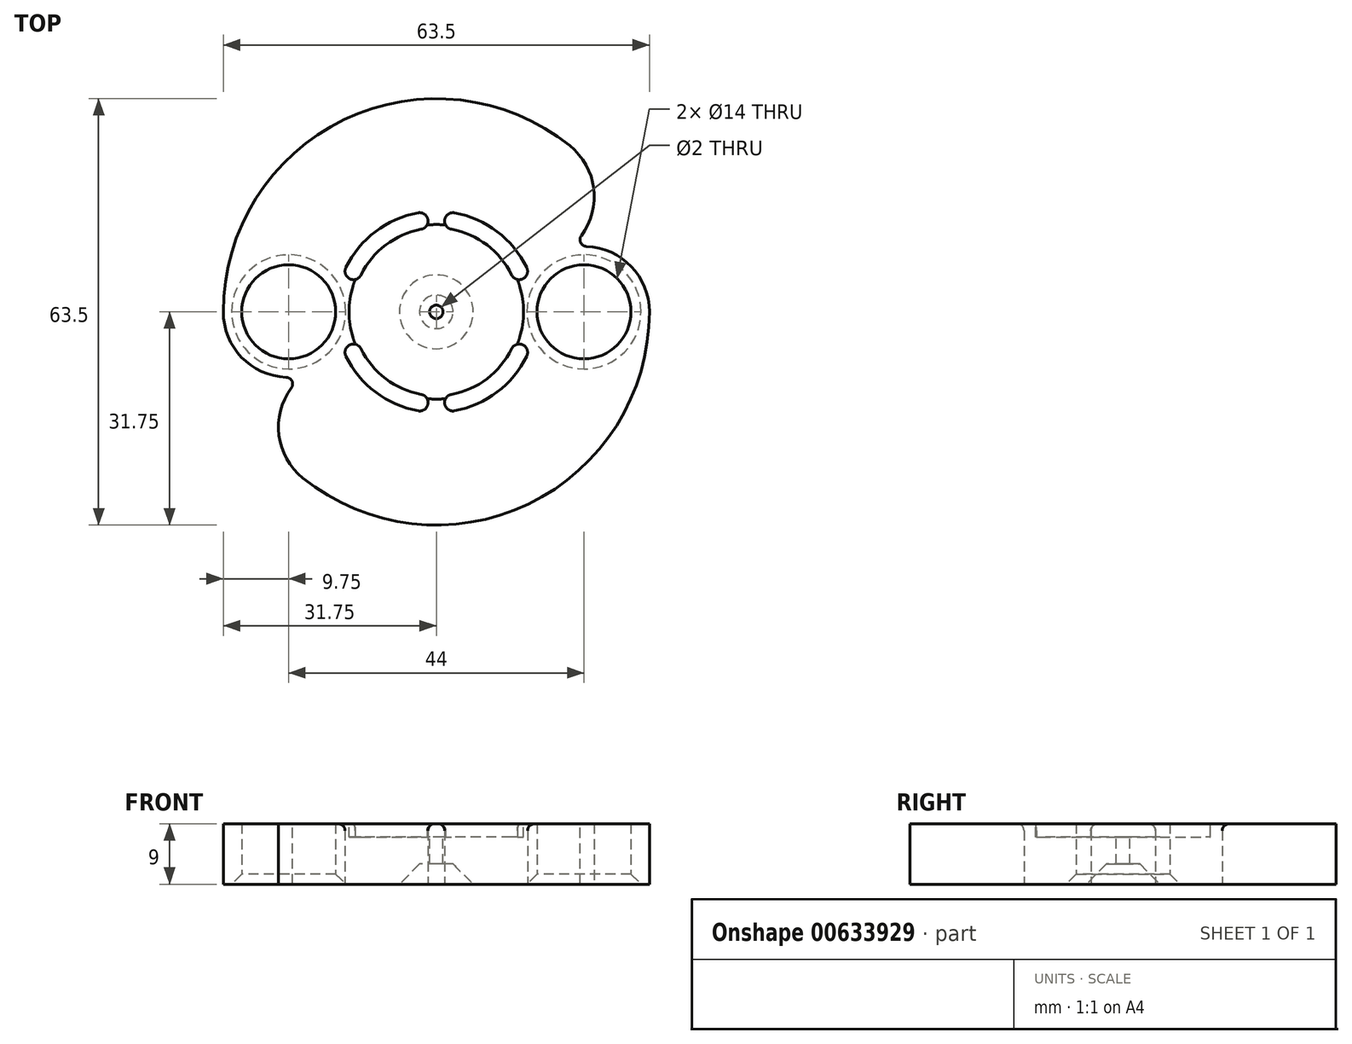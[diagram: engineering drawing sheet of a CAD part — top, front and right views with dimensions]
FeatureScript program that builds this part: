
annotation { "Feature Type Name" : "Feature", "Feature Type Description" : "" }
export const myFeature = defineFeature(function(context is Context, id is Id, definition is map)
    precondition{}
    {
        {
            var Q0;
            Q0=qCreatedBy(makeId("Top.planeOp"),FACE);
            var sketch = newSketch(context, id + "F0", { "sketchPlane" : qUnion([Q0])});
            skCircle(sketch, "E0", {"center": v(0, 0) * mm, "radius": 32.5 * mm});
            skCircle(sketch, "E1", {"center": v(0, 0) * mm, "radius": 2.5 * mm});
            skCircle(sketch, "E2", {"center": v(22, 0) * mm, "radius": 7 * mm});
            skLineSegment(sketch, "E3", {"start": v(0, 0) * mm, "end": v(22, 0) * mm, "construction": true});
            skLineSegment(sketch, "E4", {"start": v(0, 0) * mm, "end": v(-22, 0) * mm, "construction": true});
            skCircle(sketch, "E5", {"center": v(-22, 0) * mm, "radius": 7 * mm});
            skSolve(sketch);
        }
        {
            var Q0;
            Q0 = qSketchRegion(id + "F0", true);
            extrude(context, id + "F1", {"entities" : qUnion([Q0]), "endBound" : BoundingType.SYMMETRIC, "depth" : 9 * mm, "offsetDistance" : 25 * mm});
        }
        {
            var Q0;
            Q0=makeQuery(id+"F1.opExtrude","CAP_FACE",FACE,{"disambiguationData":[OSD([sQuery(id+"F0.wireOp",EDGE,"E0"),sQuery(id+"F0.wireOp",EDGE,"E1"),sQuery(id+"F0.wireOp",EDGE,"E2")])],"isStart":false});
            var sketch = newSketch(context, id + "F2", { "sketchPlane" : qUnion([Q0])});
            skCircle(sketch, "E6", {"center": v(0, 0) * mm, "radius": 1 * mm});
            skCircle(sketch, "E7", {"center": v(0, 0) * mm, "radius": 2.5 * mm});
            skSolve(sketch);
        }
        {
            var Q0;
            Q0 = qSketchRegion(id + "F2", true);
            extrude(context, id + "F3", {"entities" : qUnion([Q0]), "operationType" : NewBodyOperationType.ADD, "oppositeDirection" : true, "depth" : 6 * mm, "offsetDistance" : 25 * mm});
        }
        {
            var Q0;
            Q0=makeQuery(id+"F1.opExtrude","CAP_FACE",FACE,{"disambiguationData":[OSD([sQuery(id+"F0.wireOp",EDGE,"E0"),sQuery(id+"F0.wireOp",EDGE,"E1"),sQuery(id+"F0.wireOp",EDGE,"E2")])],"isStart":true});
            var sketch = newSketch(context, id + "F4", { "sketchPlane" : qUnion([Q0])});
            skLineSegment(sketch, "E8", {"start": v(0, 0) * mm, "end": v(22, 0) * mm, "construction": true});
            skCircle(sketch, "E9", {"center": v(0, 0) * mm, "radius": 32.5 * mm});
            skArc(sketch, "E10", {"start": v(12.25, 0) * mm, "mid": v(5.3, 11.05) * mm, "end": v(-7.67, 9.55) * mm});
            skArc(sketch, "E11", {"start": v(31.75, 0) * mm, "mid": v(13.72, 28.63) * mm, "end": v(-19.9, 24.75) * mm});
            skLineSegment(sketch, "E12", {"start": v(0, 0) * mm, "end": v(-22, 0) * mm, "construction": true});
            skArc(sketch, "E13", {"start": v(-12.25, 0) * mm, "mid": v(-22, 9.75) * mm, "end": v(-31.75, 0) * mm});
            skArc(sketch, "E14", {"start": v(12.25, 0) * mm, "mid": v(22, -9.75) * mm, "end": v(31.75, 0) * mm});
            skCircle(sketch, "E15", {"center": v(0, 0) * mm, "radius": 22 * mm, "construction": true});
            skArc(sketch, "E16", {"start": v(-15.94, 7.64) * mm, "mid": v(-11.6, 7.65) * mm, "end": v(-7.67, 9.55) * mm});
            skArc(sketch, "E17.trimOffspring", {"start": v(-19.9, 24.75) * mm, "mid": v(-23.53, 17.12) * mm, "end": v(-19.84, 9.5) * mm});
            skArc(sketch, "E18", {"start": v(15.94, -7.64) * mm, "mid": v(11.6, -7.65) * mm, "end": v(7.67, -9.55) * mm});
            skArc(sketch, "E19.trimOffspring", {"start": v(19.9, -24.75) * mm, "mid": v(23.53, -17.12) * mm, "end": v(19.84, -9.5) * mm});
            skArc(sketch, "E20.trimOffspring", {"start": v(-12.25, 0) * mm, "mid": v(-5.3, -11.05) * mm, "end": v(7.67, -9.55) * mm});
            skArc(sketch, "E21.trimOffspring", {"start": v(-31.75, 0) * mm, "mid": v(-13.72, -28.63) * mm, "end": v(19.9, -24.75) * mm});
            skSolve(sketch);
        }
        {
            var Q0;
            Q0 = qSketchRegion(id + "F4", true);
            extrude(context, id + "F5", {"entities" : qUnion([Q0]), "operationType" : NewBodyOperationType.REMOVE, "oppositeDirection" : true, "depth" : 5 * mm, "offsetDistance" : 25 * mm});
        }
        {
            var Q0;
            Q0=makeQuery(id+"F3.boolean.opBoolean","MERGE",FACE,{"derivedFrom":[makeQuery(id+"F1.opExtrude","CAP_FACE",FACE,{"disambiguationData":[OSD([sQuery(id+"F0.wireOp",EDGE,"E0"),sQuery(id+"F0.wireOp",EDGE,"E1"),sQuery(id+"F0.wireOp",EDGE,"E2")])],"isStart":false}),makeQuery(id+"F3.opExtrude","CAP_FACE",FACE,{"disambiguationData":[OSD([sQuery(id+"F2.wireOp",EDGE,"E6"),sQuery(id+"F2.wireOp",EDGE,"E7")])],"isStart":true})]});
            var sketch = newSketch(context, id + "F6", { "sketchPlane" : qUnion([Q0])});
            skCircle(sketch, "E22", {"center": v(0, 0) * mm, "radius": 13 * mm});
            skSolve(sketch);
        }
        {
            var Q0;
            Q0 = qSketchRegion(id + "F6", true);
            extrude(context, id + "F7", {"entities" : qUnion([Q0]), "operationType" : NewBodyOperationType.REMOVE, "oppositeDirection" : true, "depth" : 2 * mm, "offsetDistance" : 25 * mm});
        }
        {
            var Q0;
            Q0 = qSketchRegion(id + "F6", true);
            extrude(context, id + "F8", {"entities" : qUnion([Q0]), "operationType" : NewBodyOperationType.REMOVE, "oppositeDirection" : true, "depth" : 2 * mm, "offsetDistance" : 25 * mm});
        }
        {
            var Q0;
            Q0=makeQuery(id+"F5.boolean.opBoolean","COPY",FACE,{"derivedFrom":makeQuery(id+"F5.opExtrude","CAP_FACE",FACE,{"disambiguationData":[OSD([sQuery(id+"F4.wireOp",EDGE,"E9"),sQuery(id+"F4.wireOp",EDGE,"E11"),sQuery(id+"F4.wireOp",EDGE,"E13"),sQuery(id+"F4.wireOp",EDGE,"E14"),sQuery(id+"F4.wireOp",EDGE,"E17.trimOffspring"),sQuery(id+"F4.wireOp",EDGE,"E19.trimOffspring"),sQuery(id+"F4.wireOp",EDGE,"E21.trimOffspring")])],"isStart":false})});
            var sketch = newSketch(context, id + "F9", { "sketchPlane" : qUnion([Q0])});
            skArc(sketch, "E23", {"start": v(19.84, -9.5) * mm, "mid": v(28.08, -7.62) * mm, "end": v(31.75, 0) * mm});
            skArc(sketch, "E24", {"start": v(-19.84, 9.5) * mm, "mid": v(-28.08, 7.62) * mm, "end": v(-31.75, 0) * mm});
            skArc(sketch, "E25", {"start": v(-19.9, 24.75) * mm, "mid": v(-23.53, 17.12) * mm, "end": v(-19.84, 9.5) * mm});
            skArc(sketch, "E26", {"start": v(31.75, 0) * mm, "mid": v(13.72, 28.63) * mm, "end": v(-19.9, 24.75) * mm});
            skCircle(sketch, "E27", {"center": v(0, 0) * mm, "radius": 32.5 * mm});
            skArc(sketch, "E28.trimOffspring", {"start": v(-31.75, 0) * mm, "mid": v(-13.72, -28.63) * mm, "end": v(19.9, -24.75) * mm});
            skArc(sketch, "E29", {"start": v(19.9, -24.75) * mm, "mid": v(23.53, -17.12) * mm, "end": v(19.84, -9.5) * mm});
            skSolve(sketch);
        }
        {
            var Q0;
            Q0 = qSketchRegion(id + "F9", true);
            extrude(context, id + "F10", {"entities" : qUnion([Q0]), "operationType" : NewBodyOperationType.REMOVE, "endBound" : BoundingType.THROUGH_ALL, "oppositeDirection" : true, "depth" : 25 * mm, "offsetDistance" : 25 * mm});
        }
        {
            var Q0;
            Q0=makeQuery(id+"F1.opExtrude","CAP_FACE",FACE,{"disambiguationData":[OSD([sQuery(id+"F0.wireOp",EDGE,"E0"),sQuery(id+"F0.wireOp",EDGE,"E1"),sQuery(id+"F0.wireOp",EDGE,"E2"),sQuery(id+"F0.wireOp",EDGE,"E5")])],"isStart":true});
            var sketch = newSketch(context, id + "F11", { "sketchPlane" : qUnion([Q0])});
            skArc(sketch, "E30", {"start": v(2.71, -14.75) * mm, "mid": v(9.07, -11.95) * mm, "end": v(13.48, -6.59) * mm});
            skArc(sketch, "E31", {"start": v(2.26, -12.3) * mm, "mid": v(7.55, -9.96) * mm, "end": v(11.23, -5.49) * mm});
            skArc(sketch, "E32", {"start": v(11.23, 5.49) * mm, "mid": v(12.9, 4.92) * mm, "end": v(13.48, 6.59) * mm});
            skArc(sketch, "E33", {"start": v(13.48, -6.59) * mm, "mid": v(12.9, -4.92) * mm, "end": v(11.23, -5.49) * mm});
            skArc(sketch, "E34", {"start": v(-2.71, -14.75) * mm, "mid": v(-1.26, -13.75) * mm, "end": v(-2.26, -12.3) * mm});
            skArc(sketch, "E35", {"start": v(2.26, -12.3) * mm, "mid": v(1.26, -13.75) * mm, "end": v(2.71, -14.75) * mm});
            skArc(sketch, "E36", {"start": v(-2.26, 12.3) * mm, "mid": v(-1.26, 13.75) * mm, "end": v(-2.71, 14.75) * mm});
            skArc(sketch, "E37", {"start": v(2.71, 14.75) * mm, "mid": v(1.26, 13.75) * mm, "end": v(2.26, 12.3) * mm});
            skArc(sketch, "E38.trimOffspring", {"start": v(11.23, 5.49) * mm, "mid": v(7.55, 9.96) * mm, "end": v(2.26, 12.3) * mm});
            skArc(sketch, "E39.trimOffspring", {"start": v(13.48, 6.59) * mm, "mid": v(9.07, 11.95) * mm, "end": v(2.71, 14.75) * mm});
            skArc(sketch, "E40.trimOffspring", {"start": v(-2.26, 12.3) * mm, "mid": v(-7.55, 9.96) * mm, "end": v(-11.23, 5.5) * mm});
            skArc(sketch, "E41.trimOffspring", {"start": v(-2.71, 14.75) * mm, "mid": v(-9.06, 11.95) * mm, "end": v(-13.47, 6.6) * mm});
            skArc(sketch, "E42.trimOffspring", {"start": v(-13.48, -6.59) * mm, "mid": v(-9.07, -11.95) * mm, "end": v(-2.71, -14.75) * mm});
            skArc(sketch, "E43.trimOffspring", {"start": v(-11.23, -5.49) * mm, "mid": v(-7.55, -9.96) * mm, "end": v(-2.26, -12.3) * mm});
            skArc(sketch, "E44", {"start": v(-11.23, -5.49) * mm, "mid": v(-12.9, -4.92) * mm, "end": v(-13.48, -6.59) * mm});
            skArc(sketch, "E45", {"start": v(-13.47, 6.6) * mm, "mid": v(-12.9, 4.92) * mm, "end": v(-11.23, 5.5) * mm});
            skSolve(sketch);
        }
        {
            var Q0;
            Q0 = qSketchRegion(id + "F11", true);
            extrude(context, id + "F12", {"entities" : qUnion([Q0]), "operationType" : NewBodyOperationType.REMOVE, "endBound" : BoundingType.THROUGH_ALL, "oppositeDirection" : true, "depth" : 25 * mm, "offsetDistance" : 25 * mm});
        }
        {
            var Q0;
            Q0=makeQuery(id+"F1.opExtrude","CAP_EDGE",EDGE,{"disambiguationData":[OSD([sQuery(id+"F0.wireOp",EDGE,"E2")])],"isStart":true});
            var Q1;
            Q1=makeQuery(id+"F1.opExtrude","CAP_EDGE",EDGE,{"disambiguationData":[OSD([sQuery(id+"F0.wireOp",EDGE,"E5")])],"isStart":true});
            chamfer(context, id + "F13", {"entities" : qUnion([Q0, Q1]), "width" : 1.5 * mm, "tangentPropagation" : true});
        }
        {
            var Q0;
            Q0=makeQuery(id+"F10.boolean.opBoolean","MERGE",EDGE,{"derivedFrom":[makeQuery(id+"F5.boolean.opBoolean","COPY",EDGE,{"derivedFrom":makeQuery(id+"F5.opExtrude","SWEPT_EDGE",EDGE,{"disambiguationData":[OSD([sQuery(id+"F4.wireOp",EDGE,"E13"),sQuery(id+"F4.wireOp",EDGE,"E17.trimOffspring")])]})}),makeQuery(id+"F10.opExtrude","SWEPT_EDGE",EDGE,{"disambiguationData":[OSD([sQuery(id+"F9.wireOp",EDGE,"E24"),sQuery(id+"F9.wireOp",EDGE,"E25")])]})]});
            var Q1;
            Q1=makeQuery(id+"F10.boolean.opBoolean","MERGE",EDGE,{"derivedFrom":[makeQuery(id+"F5.boolean.opBoolean","COPY",EDGE,{"derivedFrom":makeQuery(id+"F5.opExtrude","SWEPT_EDGE",EDGE,{"disambiguationData":[OSD([sQuery(id+"F4.wireOp",EDGE,"E14"),sQuery(id+"F4.wireOp",EDGE,"E19.trimOffspring")])]})}),makeQuery(id+"F10.opExtrude","SWEPT_EDGE",EDGE,{"disambiguationData":[OSD([sQuery(id+"F9.wireOp",EDGE,"E23"),sQuery(id+"F9.wireOp",EDGE,"E29")])]})]});
            fillet(context, id + "F14", {"entities" : qUnion([Q0, Q1]), "radius" : 1 * mm, "tangentPropagation" : true, "allowEdgeOverflow" : false});
        }
        {
            var Q0;
            Q0=makeQuery(id+"F12.boolean.opBoolean","INTERSECT",EDGE,{"derivedFrom":[makeQuery(id+"F3.boolean.opBoolean","MERGE",FACE,{"derivedFrom":[makeQuery(id+"F1.opExtrude","CAP_FACE",FACE,{"disambiguationData":[OSD([sQuery(id+"F0.wireOp",EDGE,"E0"),sQuery(id+"F0.wireOp",EDGE,"E1"),sQuery(id+"F0.wireOp",EDGE,"E2"),sQuery(id+"F0.wireOp",EDGE,"E5")])],"isStart":false}),makeQuery(id+"F3.opExtrude","CAP_FACE",FACE,{"disambiguationData":[OSD([sQuery(id+"F2.wireOp",EDGE,"E6"),sQuery(id+"F2.wireOp",EDGE,"E7")])],"isStart":true})]}),makeQuery(id+"F12.opExtrude","SWEPT_FACE",FACE,{"disambiguationData":[OSD([sQuery(id+"F11.wireOp",EDGE,"E42.trimOffspring")])]})]});
            var Q1;
            Q1=makeQuery(id+"F12.boolean.opBoolean","INTERSECT",EDGE,{"derivedFrom":[makeQuery(id+"F3.boolean.opBoolean","MERGE",FACE,{"derivedFrom":[makeQuery(id+"F1.opExtrude","CAP_FACE",FACE,{"disambiguationData":[OSD([sQuery(id+"F0.wireOp",EDGE,"E0"),sQuery(id+"F0.wireOp",EDGE,"E1"),sQuery(id+"F0.wireOp",EDGE,"E2"),sQuery(id+"F0.wireOp",EDGE,"E5")])],"isStart":false}),makeQuery(id+"F3.opExtrude","CAP_FACE",FACE,{"disambiguationData":[OSD([sQuery(id+"F2.wireOp",EDGE,"E6"),sQuery(id+"F2.wireOp",EDGE,"E7")])],"isStart":true})]}),makeQuery(id+"F12.opExtrude","SWEPT_FACE",FACE,{"disambiguationData":[OSD([sQuery(id+"F11.wireOp",EDGE,"E41.trimOffspring")])]})]});
            var Q2;
            Q2=makeQuery(id+"F12.boolean.opBoolean","COPY",EDGE,{"derivedFrom":makeQuery(id+"F12.opExtrude","CAP_EDGE",EDGE,{"disambiguationData":[OSD([sQuery(id+"F11.wireOp",EDGE,"E41.trimOffspring")])],"isStart":true})});
            var Q3;
            Q3=makeQuery(id+"F12.boolean.opBoolean","INTERSECT",EDGE,{"derivedFrom":[makeQuery(id+"F3.boolean.opBoolean","MERGE",FACE,{"derivedFrom":[makeQuery(id+"F1.opExtrude","CAP_FACE",FACE,{"disambiguationData":[OSD([sQuery(id+"F0.wireOp",EDGE,"E0"),sQuery(id+"F0.wireOp",EDGE,"E1"),sQuery(id+"F0.wireOp",EDGE,"E2"),sQuery(id+"F0.wireOp",EDGE,"E5")])],"isStart":false}),makeQuery(id+"F3.opExtrude","CAP_FACE",FACE,{"disambiguationData":[OSD([sQuery(id+"F2.wireOp",EDGE,"E6"),sQuery(id+"F2.wireOp",EDGE,"E7")])],"isStart":true})]}),makeQuery(id+"F12.opExtrude","SWEPT_FACE",FACE,{"disambiguationData":[OSD([sQuery(id+"F11.wireOp",EDGE,"E39.trimOffspring")])]})]});
            var Q4;
            Q4=makeQuery(id+"F12.boolean.opBoolean","COPY",EDGE,{"derivedFrom":makeQuery(id+"F12.opExtrude","CAP_EDGE",EDGE,{"disambiguationData":[OSD([sQuery(id+"F11.wireOp",EDGE,"E39.trimOffspring")])],"isStart":true})});
            var Q5;
            Q5=makeQuery(id+"F12.boolean.opBoolean","COPY",EDGE,{"derivedFrom":makeQuery(id+"F12.opExtrude","CAP_EDGE",EDGE,{"disambiguationData":[OSD([sQuery(id+"F11.wireOp",EDGE,"E30")])],"isStart":true})});
            var Q6;
            Q6=makeQuery(id+"F12.boolean.opBoolean","INTERSECT",EDGE,{"derivedFrom":[makeQuery(id+"F3.boolean.opBoolean","MERGE",FACE,{"derivedFrom":[makeQuery(id+"F1.opExtrude","CAP_FACE",FACE,{"disambiguationData":[OSD([sQuery(id+"F0.wireOp",EDGE,"E0"),sQuery(id+"F0.wireOp",EDGE,"E1"),sQuery(id+"F0.wireOp",EDGE,"E2"),sQuery(id+"F0.wireOp",EDGE,"E5")])],"isStart":false}),makeQuery(id+"F3.opExtrude","CAP_FACE",FACE,{"disambiguationData":[OSD([sQuery(id+"F2.wireOp",EDGE,"E6"),sQuery(id+"F2.wireOp",EDGE,"E7")])],"isStart":true})]}),makeQuery(id+"F12.opExtrude","SWEPT_FACE",FACE,{"disambiguationData":[OSD([sQuery(id+"F11.wireOp",EDGE,"E30")])]})]});
            var Q7;
            Q7=makeQuery(id+"F12.boolean.opBoolean","COPY",EDGE,{"derivedFrom":makeQuery(id+"F12.opExtrude","CAP_EDGE",EDGE,{"disambiguationData":[OSD([sQuery(id+"F11.wireOp",EDGE,"E42.trimOffspring")])],"isStart":true})});
            var Q8;
            Q8=makeQuery(id+"F12.boolean.opBoolean","INTERSECT",EDGE,{"derivedFrom":[makeQuery(id+"F3.boolean.opBoolean","MERGE",FACE,{"derivedFrom":[makeQuery(id+"F1.opExtrude","CAP_FACE",FACE,{"disambiguationData":[OSD([sQuery(id+"F0.wireOp",EDGE,"E0"),sQuery(id+"F0.wireOp",EDGE,"E1"),sQuery(id+"F0.wireOp",EDGE,"E2"),sQuery(id+"F0.wireOp",EDGE,"E5")])],"isStart":false}),makeQuery(id+"F3.opExtrude","CAP_FACE",FACE,{"disambiguationData":[OSD([sQuery(id+"F2.wireOp",EDGE,"E6"),sQuery(id+"F2.wireOp",EDGE,"E7")])],"isStart":true})]}),makeQuery(id+"F12.opExtrude","SWEPT_FACE",FACE,{"disambiguationData":[OSD([sQuery(id+"F11.wireOp",EDGE,"E37")])]})]});
            var Q9;
            Q9=makeQuery(id+"F12.boolean.opBoolean","INTERSECT",EDGE,{"derivedFrom":[makeQuery(id+"F3.boolean.opBoolean","MERGE",FACE,{"derivedFrom":[makeQuery(id+"F1.opExtrude","CAP_FACE",FACE,{"disambiguationData":[OSD([sQuery(id+"F0.wireOp",EDGE,"E0"),sQuery(id+"F0.wireOp",EDGE,"E1"),sQuery(id+"F0.wireOp",EDGE,"E2"),sQuery(id+"F0.wireOp",EDGE,"E5")])],"isStart":false}),makeQuery(id+"F3.opExtrude","CAP_FACE",FACE,{"disambiguationData":[OSD([sQuery(id+"F2.wireOp",EDGE,"E6"),sQuery(id+"F2.wireOp",EDGE,"E7")])],"isStart":true})]}),makeQuery(id+"F12.opExtrude","SWEPT_FACE",FACE,{"disambiguationData":[OSD([sQuery(id+"F11.wireOp",EDGE,"E36")])]})]});
            var Q10;
            Q10=makeQuery(id+"F12.boolean.opBoolean","INTERSECT",EDGE,{"derivedFrom":[makeQuery(id+"F3.boolean.opBoolean","MERGE",FACE,{"derivedFrom":[makeQuery(id+"F1.opExtrude","CAP_FACE",FACE,{"disambiguationData":[OSD([sQuery(id+"F0.wireOp",EDGE,"E0"),sQuery(id+"F0.wireOp",EDGE,"E1"),sQuery(id+"F0.wireOp",EDGE,"E2"),sQuery(id+"F0.wireOp",EDGE,"E5")])],"isStart":false}),makeQuery(id+"F3.opExtrude","CAP_FACE",FACE,{"disambiguationData":[OSD([sQuery(id+"F2.wireOp",EDGE,"E6"),sQuery(id+"F2.wireOp",EDGE,"E7")])],"isStart":true})]}),makeQuery(id+"F12.opExtrude","SWEPT_FACE",FACE,{"disambiguationData":[OSD([sQuery(id+"F11.wireOp",EDGE,"IULc2HyE-kvyv-PGGa-Ogag-i5b3ODiteL6P")])]})]});
            var Q11;
            Q11=makeQuery(id+"F12.boolean.opBoolean","INTERSECT",EDGE,{"derivedFrom":[makeQuery(id+"F3.boolean.opBoolean","MERGE",FACE,{"derivedFrom":[makeQuery(id+"F1.opExtrude","CAP_FACE",FACE,{"disambiguationData":[OSD([sQuery(id+"F0.wireOp",EDGE,"E0"),sQuery(id+"F0.wireOp",EDGE,"E1"),sQuery(id+"F0.wireOp",EDGE,"E2"),sQuery(id+"F0.wireOp",EDGE,"E5")])],"isStart":false}),makeQuery(id+"F3.opExtrude","CAP_FACE",FACE,{"disambiguationData":[OSD([sQuery(id+"F2.wireOp",EDGE,"E6"),sQuery(id+"F2.wireOp",EDGE,"E7")])],"isStart":true})]}),makeQuery(id+"F12.opExtrude","SWEPT_FACE",FACE,{"disambiguationData":[OSD([sQuery(id+"F11.wireOp",EDGE,"LXNWlSoz-vkBC-R6Zu-CKnh-kSYyZzRBl4sp")])]})]});
            var Q12;
            Q12=makeQuery(id+"F12.boolean.opBoolean","INTERSECT",EDGE,{"derivedFrom":[makeQuery(id+"F3.boolean.opBoolean","MERGE",FACE,{"derivedFrom":[makeQuery(id+"F1.opExtrude","CAP_FACE",FACE,{"disambiguationData":[OSD([sQuery(id+"F0.wireOp",EDGE,"E0"),sQuery(id+"F0.wireOp",EDGE,"E1"),sQuery(id+"F0.wireOp",EDGE,"E2"),sQuery(id+"F0.wireOp",EDGE,"E5")])],"isStart":false}),makeQuery(id+"F3.opExtrude","CAP_FACE",FACE,{"disambiguationData":[OSD([sQuery(id+"F2.wireOp",EDGE,"E6"),sQuery(id+"F2.wireOp",EDGE,"E7")])],"isStart":true})]}),makeQuery(id+"F12.opExtrude","SWEPT_FACE",FACE,{"disambiguationData":[OSD([sQuery(id+"F11.wireOp",EDGE,"E32")])]})]});
            var Q13;
            Q13=makeQuery(id+"F12.boolean.opBoolean","INTERSECT",EDGE,{"derivedFrom":[makeQuery(id+"F3.boolean.opBoolean","MERGE",FACE,{"derivedFrom":[makeQuery(id+"F1.opExtrude","CAP_FACE",FACE,{"disambiguationData":[OSD([sQuery(id+"F0.wireOp",EDGE,"E0"),sQuery(id+"F0.wireOp",EDGE,"E1"),sQuery(id+"F0.wireOp",EDGE,"E2"),sQuery(id+"F0.wireOp",EDGE,"E5")])],"isStart":false}),makeQuery(id+"F3.opExtrude","CAP_FACE",FACE,{"disambiguationData":[OSD([sQuery(id+"F2.wireOp",EDGE,"E6"),sQuery(id+"F2.wireOp",EDGE,"E7")])],"isStart":true})]}),makeQuery(id+"F12.opExtrude","SWEPT_FACE",FACE,{"disambiguationData":[OSD([sQuery(id+"F11.wireOp",EDGE,"E33")])]})]});
            var Q14;
            Q14=makeQuery(id+"F12.boolean.opBoolean","INTERSECT",EDGE,{"derivedFrom":[makeQuery(id+"F3.boolean.opBoolean","MERGE",FACE,{"derivedFrom":[makeQuery(id+"F1.opExtrude","CAP_FACE",FACE,{"disambiguationData":[OSD([sQuery(id+"F0.wireOp",EDGE,"E0"),sQuery(id+"F0.wireOp",EDGE,"E1"),sQuery(id+"F0.wireOp",EDGE,"E2"),sQuery(id+"F0.wireOp",EDGE,"E5")])],"isStart":false}),makeQuery(id+"F3.opExtrude","CAP_FACE",FACE,{"disambiguationData":[OSD([sQuery(id+"F2.wireOp",EDGE,"E6"),sQuery(id+"F2.wireOp",EDGE,"E7")])],"isStart":true})]}),makeQuery(id+"F12.opExtrude","SWEPT_FACE",FACE,{"disambiguationData":[OSD([sQuery(id+"F11.wireOp",EDGE,"E35")])]})]});
            fillet(context, id + "F15", {"entities" : qUnion([Q0, Q1, Q2, Q3, Q4, Q5, Q6, Q7, Q8, Q9, Q10, Q11, Q12, Q13, Q14]), "radius" : 1 * mm, "tangentPropagation" : true, "allowEdgeOverflow" : false});
        }
        {
            var Q0;
            Q0=makeQuery(id+"F1.opExtrude","CAP_EDGE",EDGE,{"disambiguationData":[OSD([sQuery(id+"F0.wireOp",EDGE,"E1")])],"isStart":true});
            chamfer(context, id + "F16", {"entities" : qUnion([Q0]), "chamferType" : ChamferType.OFFSET_ANGLE, "width" : 3 * mm, "oppositeDirection" : false, "angle" : 45 * degree, "tangentPropagation" : true});
        }
    });
